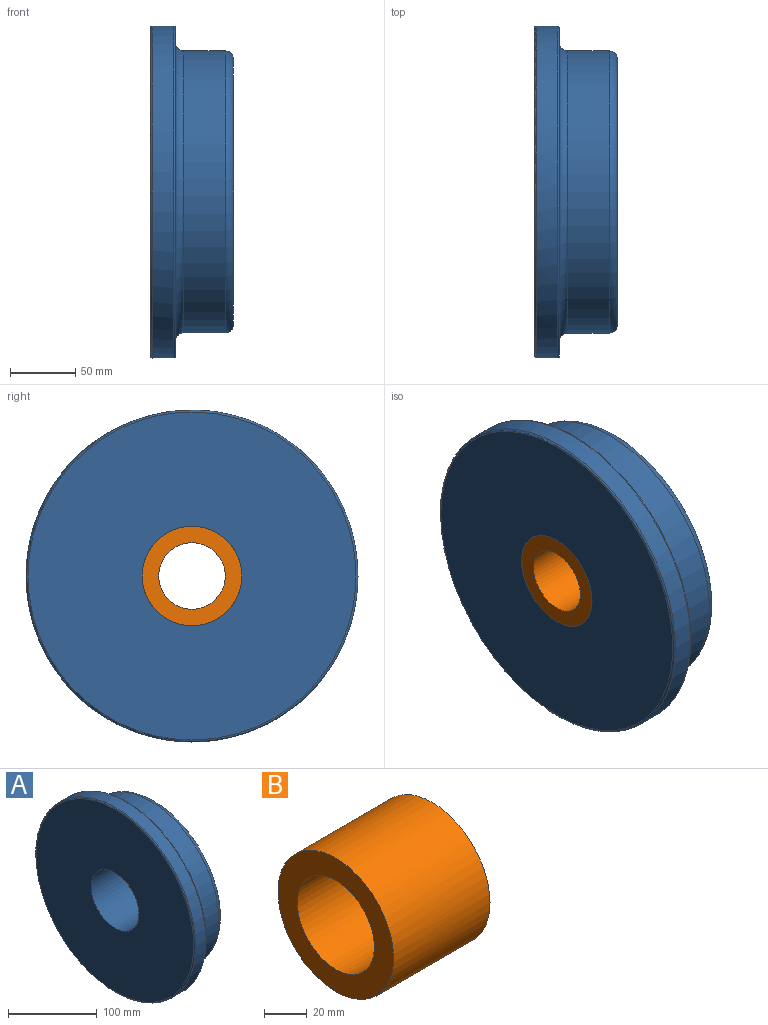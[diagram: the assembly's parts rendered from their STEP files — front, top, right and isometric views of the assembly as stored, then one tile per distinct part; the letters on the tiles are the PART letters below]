
ASSEMBLY  parts=2 mates=1
PART A: 10 faces, bbox 63.5x274.9x274.9 mm
  f0: plane 203.2x203.2mm, normal (1,0,0), area 27868.9mm2, adj f1,f7
  f1: cylinder r=38.1mm len=76.2mm, axis (-1,0,0), area 15201.2mm2, adj f0,f2
  f2: plane 250.95x250.95mm, normal (-1,0,0), area 44901.6mm2, adj f1,f8
  f3: cylinder r=127mm len=254mm, axis (-1,0,0), area 12769mm2, adj f8,f9
  f4: plane 250.95x250.95mm, normal (1,0,0), area 8418.6mm2, adj f6,f9
  f5: cylinder r=107.95mm len=215.9mm, axis (-1,0,0), area 21535.1mm2, adj f6,f7
  f6: torus R=114.3mm, axis (-1,0,0), area 6910.1mm2, adj f4,f5
  f7: torus R=101.6mm, axis (-1,0,0), area 6620.8mm2, adj f0,f5
  f8: torus R=125.48mm, axis (1,0,0), area 1901.9mm2, adj f2,f3
  f9: torus R=125.48mm, axis (-1,0,0), area 1901.9mm2, adj f3,f4
PART B: 4 faces, bbox 63.5x76.2x76.2 mm
  f0: plane 76.2x76.2mm, normal (-1,0,0), area 2529.5mm2, adj f2,f3
  f1: plane 76.2x76.2mm, normal (1,0,0), area 2529.5mm2, adj f2,f3
  f2: cylinder r=38.1mm len=76.2mm, axis (1,0,0), area 15201.2mm2, adj f0,f1
  f3: cylinder r=25.43mm len=63.5mm, axis (1,0,0), area 10144.3mm2, adj f0,f1
PLACE A at identity
PLACE B at identity
MATE fastened B.f2 <-> A.f1  axis (-1,0,0) through (0,0,0)mm
